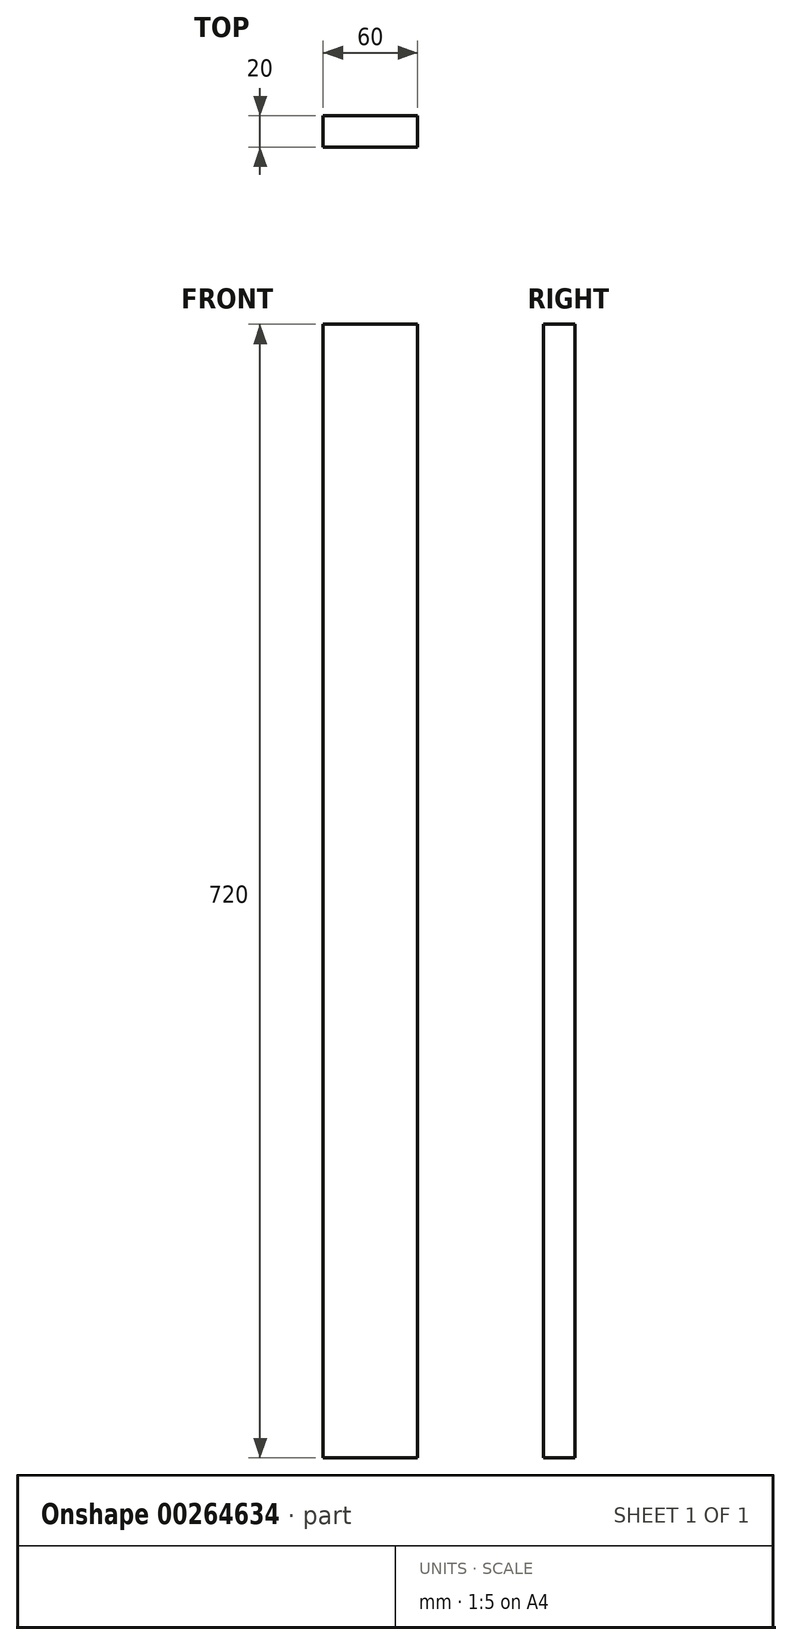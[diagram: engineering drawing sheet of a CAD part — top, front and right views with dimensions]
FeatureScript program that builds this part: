
annotation { "Feature Type Name" : "Feature", "Feature Type Description" : "" }
export const myFeature = defineFeature(function(context is Context, id is Id, definition is map)
    precondition{}
    {
        {
            var Q0;
            Q0=qCreatedBy(makeId("Front.planeOp"),FACE);
            var sketch = newSketch(context, id + "F0", { "sketchPlane" : qUnion([Q0])});
            skLineSegment(sketch, "E0", {"start": v(0, 0) * mm, "end": v(30, 0) * mm});
            skLineSegment(sketch, "E1", {"start": v(30, 0) * mm, "end": v(30, 720) * mm});
            skLineSegment(sketch, "E2", {"start": v(30, 720) * mm, "end": v(-30, 720) * mm});
            skLineSegment(sketch, "E3", {"start": v(-30, 720) * mm, "end": v(-30, 0) * mm});
            skLineSegment(sketch, "E4", {"start": v(-30, 0) * mm, "end": v(0, 0) * mm});
            skSolve(sketch);
        }
        {
            var Q0;
            Q0=makeQuery(id+"F0.imprint","IMPRINT",FACE,{"disambiguationData":[TD([[makeQuery(id+"F0.imprint","IMPRINT",EDGE,{"derivedFrom":sQuery(id+"F0.wireOp",EDGE,"E0")}),1.0]])]});
            extrude(context, id + "F1", {"entities" : qUnion([Q0]), "depth" : 20 * mm});
        }
    });
